# Revit family: TWR_Ceiling_Based_v_1.01
name_source: partatom
category: Windows
revit_build: Autodesk Revit MEP 2012 (Build: 20110309_2315(x64)
units: mm (PartAtom-declared; Revit-internal decimal feet)

## types (2) — shared parameters
Assembly Code = B3020110
BIMobject Category = Roof Window
BIMobject QR code url = http://velux.bimobject.com
Date of publishing = 6/4/2013
Design country = Denmark
Edition number = 1
Emergency Exit = Yes
IFC Classification = Window
Installation instructions = http://www.velux.co.uk
Manufacturer = VELUX A/S
Manufacturer URL = www.velux.com
Manufacturer country = Denmark
Material main = Aluminum, Anodized Silver
Max Height = 6 meters
Model = Velux sun tunnel TWR
NBS Reference = 59-72
NBS Reference Description = Roof Window Units
Name of the object = Velux sun tunnel TWR
Product SKU = twr
Product data url = http://www.velux.co.uk
Product family = Sun tunnel
Product group = TWR
UNSPC Category = Roofing accessories
UNSPC code = 301516
URL = http://velux.bimobject.com
Uniclass 1.4 Code = JL11
Uniclass 1.4 Description = Rooflights/Roof windows
Uniclass 2.0 Code = PR-59-72
Uniclass 2.0 Description = Roof Window Units
zero-valued in all types: Frame Area, Perimeter Glazing, Perimeter Window, Sound Insulation db, Thermal Transmittance(frame), Thermal bridge(glazing), Window Area

## per-type parameters (varying)
| type | Ceiling Frame Inner Diameter | Ceiling Frame Inner Radius | Ceiling Frame Outer Diameter | Ceiling Frame Outer Radius | Ceiling Opening Diameter | Ceiling Opening Radius | Flex Inner Radius | Flex Radius | Frame Radius | Material secondary |
| Flex 175R | 336 mm  [stored 1.10236 ft] | 168 mm  [stored 0.551181 ft] | 430 mm | 215 mm | 400 mm  [stored 1.31234 ft] | 200 mm  [stored 0.656168 ft] | 170 mm  [stored 0.557743 ft] | 175 mm  [stored 0.574147 ft] | 170 mm  [stored 0.557743 ft] | Glass 73Q + ISD 0000 |
| Flex 125R | 236 mm | 118 mm | 330 mm | 165 mm | 300 mm | 150 mm  [stored 0.492126 ft] | 120 mm  [stored 0.393701 ft] | 125 mm  [stored 0.410105 ft] | 120 mm  [stored 0.393701 ft] | Acrylic, frosted |

note: [stored X ft] marks values corroborated as IEEE doubles in the binary element streams (Revit-internal decimal feet)

## geometry (parser evidence)
native form markers: Blend x38, Sweep x3
no freeform markers — native parametric forms only
